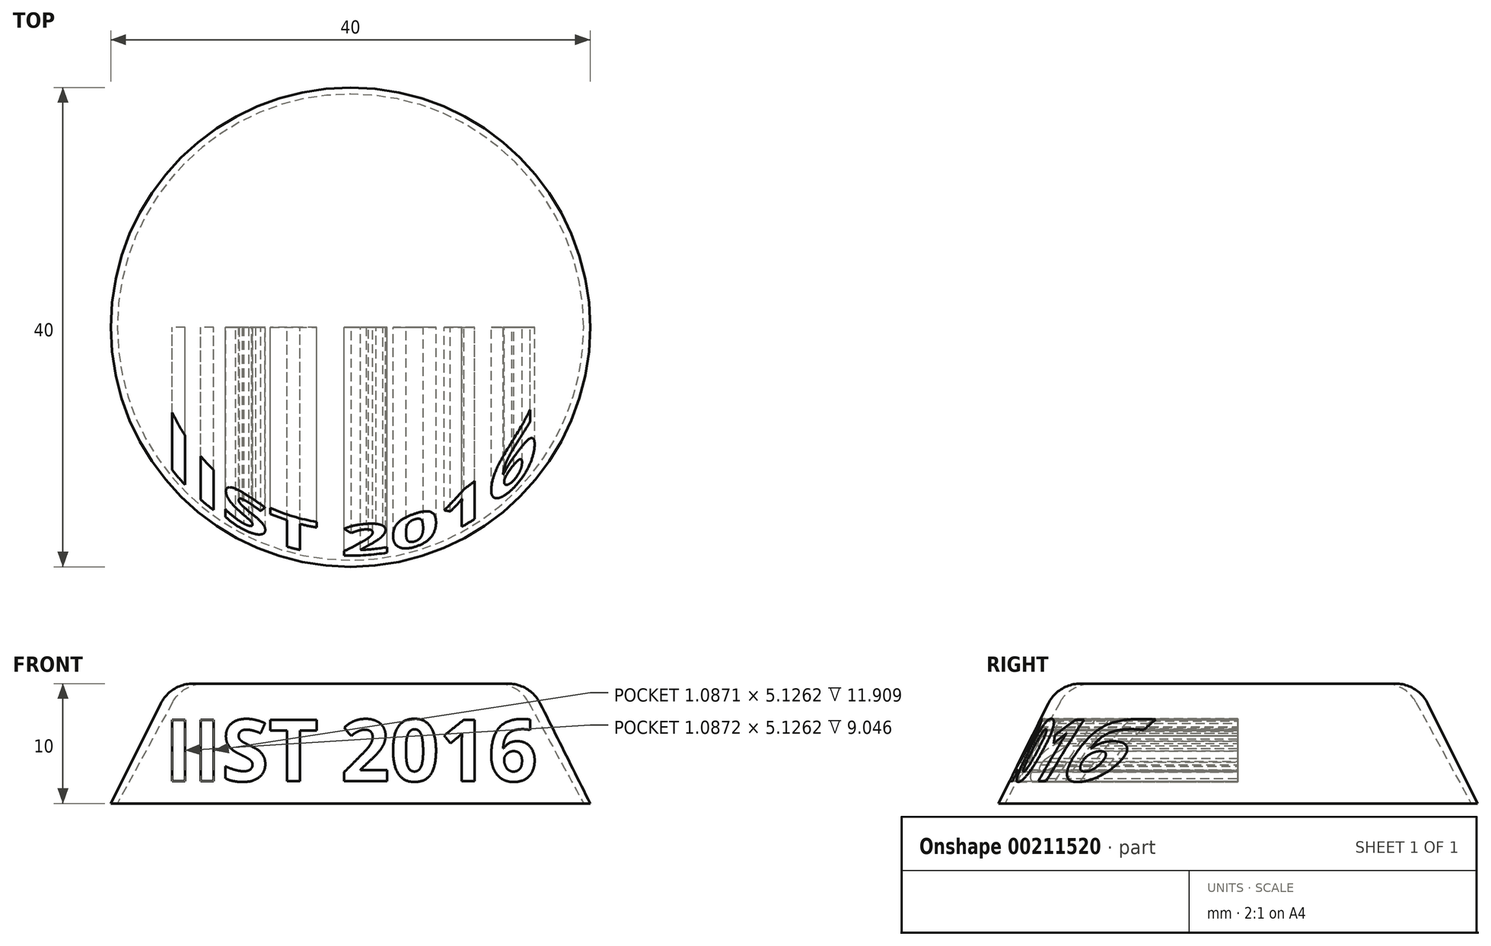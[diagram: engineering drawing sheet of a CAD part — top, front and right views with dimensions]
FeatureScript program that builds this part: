
annotation { "Feature Type Name" : "Feature", "Feature Type Description" : "" }
export const myFeature = defineFeature(function(context is Context, id is Id, definition is map)
    precondition{}
    {
        {
            var Q0;
            Q0=qCreatedBy(makeId("Top.planeOp"),FACE);
            var sketch = newSketch(context, id + "F0", { "sketchPlane" : qUnion([Q0])});
            skCircle(sketch, "E0", {"center": v(0, 0) * mm, "radius": 20 * mm});
            skSolve(sketch);
        }
        {
            var Q0;
            Q0 = qSketchRegion(id + "F0", true);
            extrude(context, id + "F1", {"entities" : qUnion([Q0]), "depth" : 10 * mm});
        }
        {
            var Q0;
            Q0=makeQuery(id+"F1.opExtrude","CAP_EDGE",EDGE,{"disambiguationData":[OSD([sQuery(id+"F0.wireOp",EDGE,"E0")])],"isStart":false});
            chamfer(context, id + "F2", {"entities" : qUnion([Q0]), "chamferType" : ChamferType.TWO_OFFSETS, "width1" : 5 * mm, "oppositeDirection" : false, "width2" : 10 * mm, "tangentPropagation" : true});
        }
        {
            var Q0;
            Q0=qCreatedBy(makeId("Front.planeOp"),FACE);
            var sketch = newSketch(context, id + "F3", { "sketchPlane" : qUnion([Q0])});
            skText(sketch, "E1", { "text": "IIST 2016", "fontName": "OpenSans-Bold.ttf"});
            const initialGuessF3  = {"E1": [-0.01554, 0.00186, 1, 0, 0.00517]};
            skSetInitialGuess(sketch, initialGuessF3);
            skSolve(sketch);
        }
        {
            var Q0;
            Q0 = qSketchRegion(id + "F3", true);
            extrude(context, id + "F4", {"entities" : qUnion([Q0]), "operationType" : NewBodyOperationType.REMOVE, "depth" : 25 * mm});
        }
        {
            var Q0;
            {var subQ0=sQuery(id+"F0.wireOp",EDGE,"E0");Q0=makeQuery(id+"F2.opChamfer","BLEND_EDGE",EDGE,{"blendedFrom":[makeQuery(id+"F1.opExtrude","CAP_EDGE",EDGE,{"disambiguationData":[OSD([subQ0])],"isStart":false}),makeQuery(id+"F1.opExtrude","CAP_FACE",FACE,{"disambiguationData":[OSD([subQ0])],"isStart":false})],"blendedInto":[makeQuery(id+"F1.opExtrude","CAP_FACE",FACE,{"disambiguationData":[OSD([subQ0])],"isStart":false})]});}
            fillet(context, id + "F5", {"entities" : qUnion([Q0]), "radius" : 3 * mm, "tangentPropagation" : true, "allowEdgeOverflow" : false});
        }
        {
            var Q0;
            Q0=qCreatedBy(makeId("Top.planeOp"),FACE);
            var sketch = newSketch(context, id + "F6", { "sketchPlane" : qUnion([Q0])});
            skCircle(sketch, "E2", {"center": v(0, 0) * mm, "radius": 20 * mm});
            skSolve(sketch);
        }
        {
            var Q0;
            Q0 = qSketchRegion(id + "F6", true);
            extrude(context, id + "F7", {"entities" : qUnion([Q0]), "depth" : 10 * mm});
        }
        {
            var Q0;
            Q0=makeQuery(id+"F7.opExtrude","CAP_EDGE",EDGE,{"disambiguationData":[OSD([sQuery(id+"F6.wireOp",EDGE,"E2")])],"isStart":false});
            chamfer(context, id + "F8", {"entities" : qUnion([Q0]), "chamferType" : ChamferType.TWO_OFFSETS, "width1" : 6 * mm, "oppositeDirection" : false, "width2" : 11 * mm, "tangentPropagation" : true});
        }
        {
            var Q0;
            Q0=makeQuery(id+"F1.opExtrude","SWEPT_BODY",BODY,{"disambiguationData":[OSD([sQuery(id+"F0.wireOp",EDGE,"E0")])]});
            transform(context, id + "F9", {"entities" : qUnion([Q0]), "transformType" : TransformType.TRANSLATION_3D, "dx" : 0 * mm, "dy" : 0 * mm, "dz" : 0 * mm, "makeCopy" : true});
        }
        {
            var Q0;
            Q0=makeQuery(id+"F9.opPattern","COPY",BODY,{"derivedFrom":makeQuery(id+"F1.opExtrude","SWEPT_BODY",BODY,{"disambiguationData":[OSD([sQuery(id+"F0.wireOp",EDGE,"E0")])]}),"instanceName":"1"});
            deleteBodies(context, id + "F10", {"entities" : qUnion([Q0])});
        }
        {
            var Q0;
            {var subQ0=sQuery(id+"F6.wireOp",EDGE,"E2");Q0=makeQuery(id+"F8.opChamfer","BLEND_EDGE",EDGE,{"blendedFrom":[makeQuery(id+"F7.opExtrude","CAP_EDGE",EDGE,{"disambiguationData":[OSD([subQ0])],"isStart":false}),makeQuery(id+"F7.opExtrude","CAP_FACE",FACE,{"disambiguationData":[OSD([subQ0])],"isStart":false})],"blendedInto":[makeQuery(id+"F7.opExtrude","CAP_FACE",FACE,{"disambiguationData":[OSD([subQ0])],"isStart":false})]});}
            fillet(context, id + "F11", {"entities" : qUnion([Q0]), "radius" : 3 * mm, "tangentPropagation" : true, "allowEdgeOverflow" : false});
        }
    });
